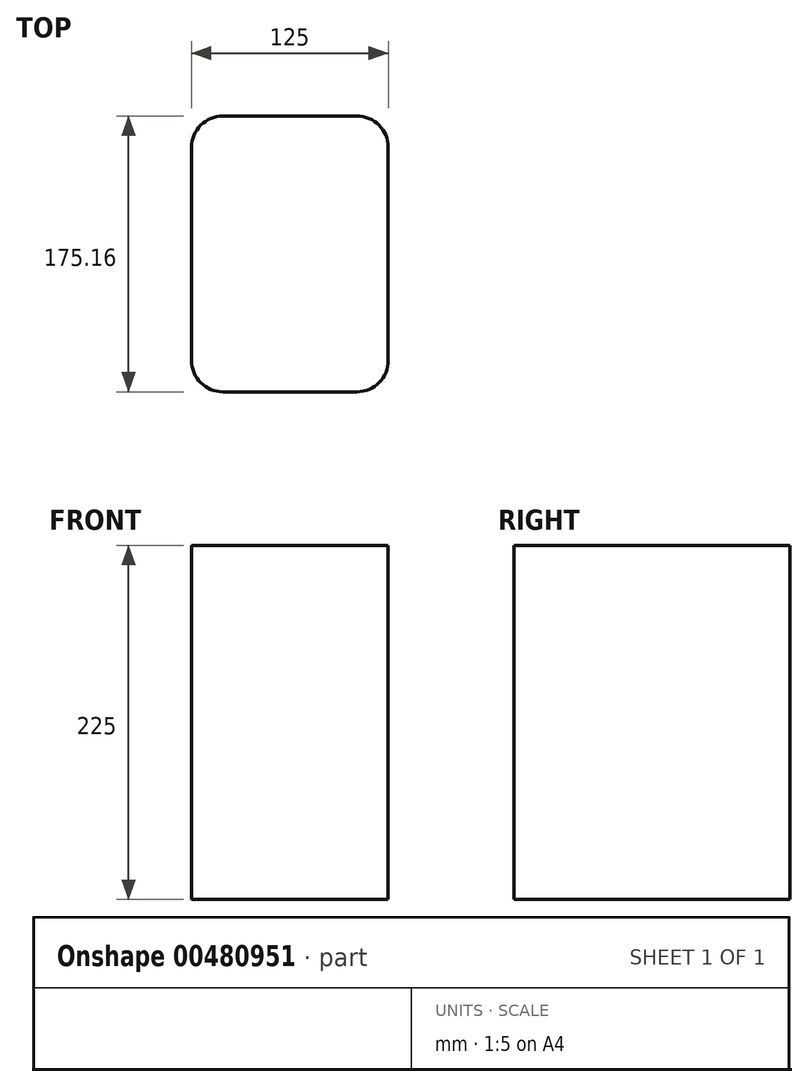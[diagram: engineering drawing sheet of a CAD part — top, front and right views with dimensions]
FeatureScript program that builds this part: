
annotation { "Feature Type Name" : "Feature", "Feature Type Description" : "" }
export const myFeature = defineFeature(function(context is Context, id is Id, definition is map)
    precondition{}
    {
        {
            var Q0;
            Q0=qCreatedBy(makeId("Top.planeOp"),FACE);
            var sketch = newSketch(context, id + "F0", { "sketchPlane" : qUnion([Q0])});
            skLineSegment(sketch, "E0", {"start": v(-48.18, 95.54) * mm, "end": v(36.82, 95.54) * mm});
            skLineSegment(sketch, "E1", {"start": v(56.82, 75.54) * mm, "end": v(56.82, -59.62) * mm});
            skLineSegment(sketch, "E2", {"start": v(36.82, -79.62) * mm, "end": v(-48.18, -79.62) * mm});
            skPoint(sketch, "E3.visualSharp", {"position": v(56.82, 95.54) * mm});
            skArc(sketch, "E3.filletArc", {"start": v(56.82, 75.54) * mm, "mid": v(50.96, 89.69) * mm, "end": v(36.82, 95.54) * mm});
            skPoint(sketch, "E4.visualSharp", {"position": v(56.82, -79.62) * mm});
            skArc(sketch, "E4.filletArc", {"start": v(36.82, -79.62) * mm, "mid": v(50.96, -73.76) * mm, "end": v(56.82, -59.62) * mm});
            skLineSegment(sketch, "E5", {"start": v(-68.18, -59.62) * mm, "end": v(-68.18, 75.54) * mm});
            skArc(sketch, "E6.filletArc", {"start": v(-48.18, 95.54) * mm, "mid": v(-62.32, 89.69) * mm, "end": v(-68.18, 75.54) * mm});
            skPoint(sketch, "E7.visualSharp", {"position": v(-68.18, -79.62) * mm});
            skArc(sketch, "E7.filletArc", {"start": v(-68.18, -59.62) * mm, "mid": v(-62.32, -73.76) * mm, "end": v(-48.18, -79.62) * mm});
            skSolve(sketch);
        }
        {
            var Q0;
            Q0 = qSketchRegion(id + "F0", true);
            extrude(context, id + "F1", {"entities" : qUnion([Q0]), "depth" : 225 * mm});
        }
    });
